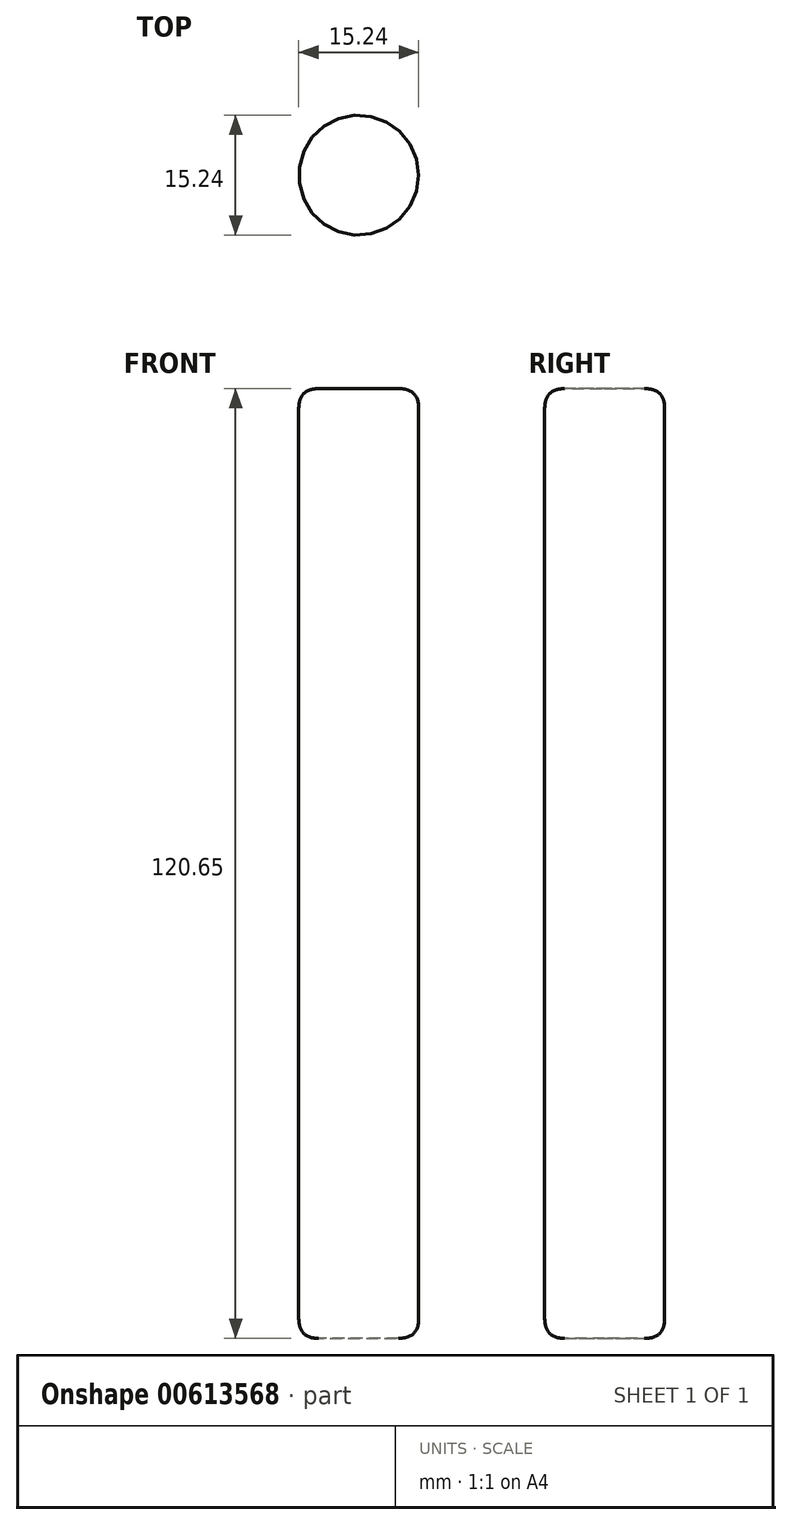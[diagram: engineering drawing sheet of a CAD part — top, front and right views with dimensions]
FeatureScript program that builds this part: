
annotation { "Feature Type Name" : "Feature", "Feature Type Description" : "" }
export const myFeature = defineFeature(function(context is Context, id is Id, definition is map)
    precondition{}
    {
        {
            var Q0;
            Q0=qCreatedBy(makeId("Top.planeOp"),FACE);
            var sketch = newSketch(context, id + "F0", { "sketchPlane" : qUnion([Q0])});
            skCircle(sketch, "E0", {"center": v(0, 0) * mm, "radius": 7.62 * mm});
            skSolve(sketch);
        }
        {
            var Q0;
            Q0 = qSketchRegion(id + "F0", true);
            extrude(context, id + "F1", {"entities" : qUnion([Q0]), "depth" : 120.65 * mm, "offsetDistance" : 25.4 * mm});
        }
        {
            var Q0;
            Q0=makeQuery(id+"F1.opExtrude","CAP_EDGE",EDGE,{"disambiguationData":[OSD([sQuery(id+"F0.wireOp",EDGE,"E0")])],"isStart":false});
            var Q1;
            Q1=makeQuery(id+"F1.opExtrude","CAP_EDGE",EDGE,{"disambiguationData":[OSD([sQuery(id+"F0.wireOp",EDGE,"E0")])],"isStart":true});
            fillet(context, id + "F2", {"entities" : qUnion([Q0, Q1]), "radius" : 2.54 * mm, "tangentPropagation" : true, "rho" : 0.5, "crossSection" : FilletCrossSection.CONIC, "allowEdgeOverflow" : false});
        }
    });
